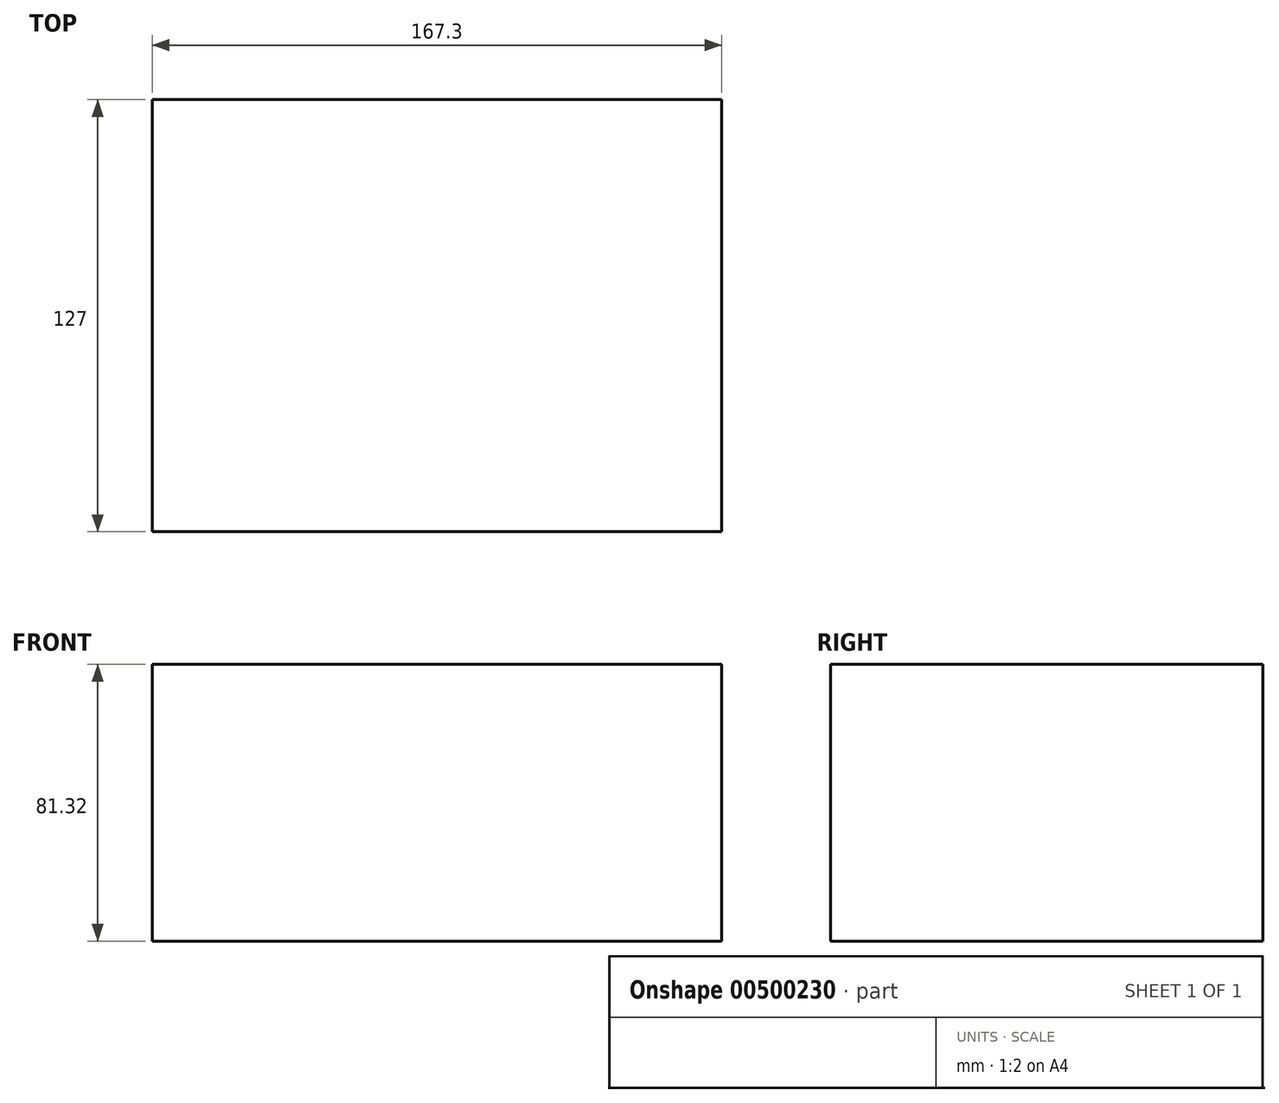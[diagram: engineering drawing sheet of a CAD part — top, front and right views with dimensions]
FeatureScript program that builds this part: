
annotation { "Feature Type Name" : "Feature", "Feature Type Description" : "" }
export const myFeature = defineFeature(function(context is Context, id is Id, definition is map)
    precondition{}
    {
        {
            var Q0;
            Q0=qCreatedBy(makeId("Front.planeOp"),FACE);
            var sketch = newSketch(context, id + "F0", { "sketchPlane" : qUnion([Q0])});
            skLineSegment(sketch, "E0.bottom", {"start": v(83.65, -40.66) * mm, "end": v(-83.65, -40.66) * mm});
            skLineSegment(sketch, "E0.top", {"start": v(83.65, 40.66) * mm, "end": v(-83.65, 40.66) * mm});
            skLineSegment(sketch, "E0.left", {"start": v(83.65, -40.66) * mm, "end": v(83.65, 40.66) * mm});
            skLineSegment(sketch, "E0.right", {"start": v(-83.65, -40.66) * mm, "end": v(-83.65, 40.66) * mm});
            skPoint(sketch, "E0.middle", {"position": v(0, 0) * mm});
            skSolve(sketch);
        }
        {
            var Q0;
            Q0 = qSketchRegion(id + "F0", true);
            extrude(context, id + "F1", {"entities" : qUnion([Q0]), "depth" : 127 * mm});
        }
    });
